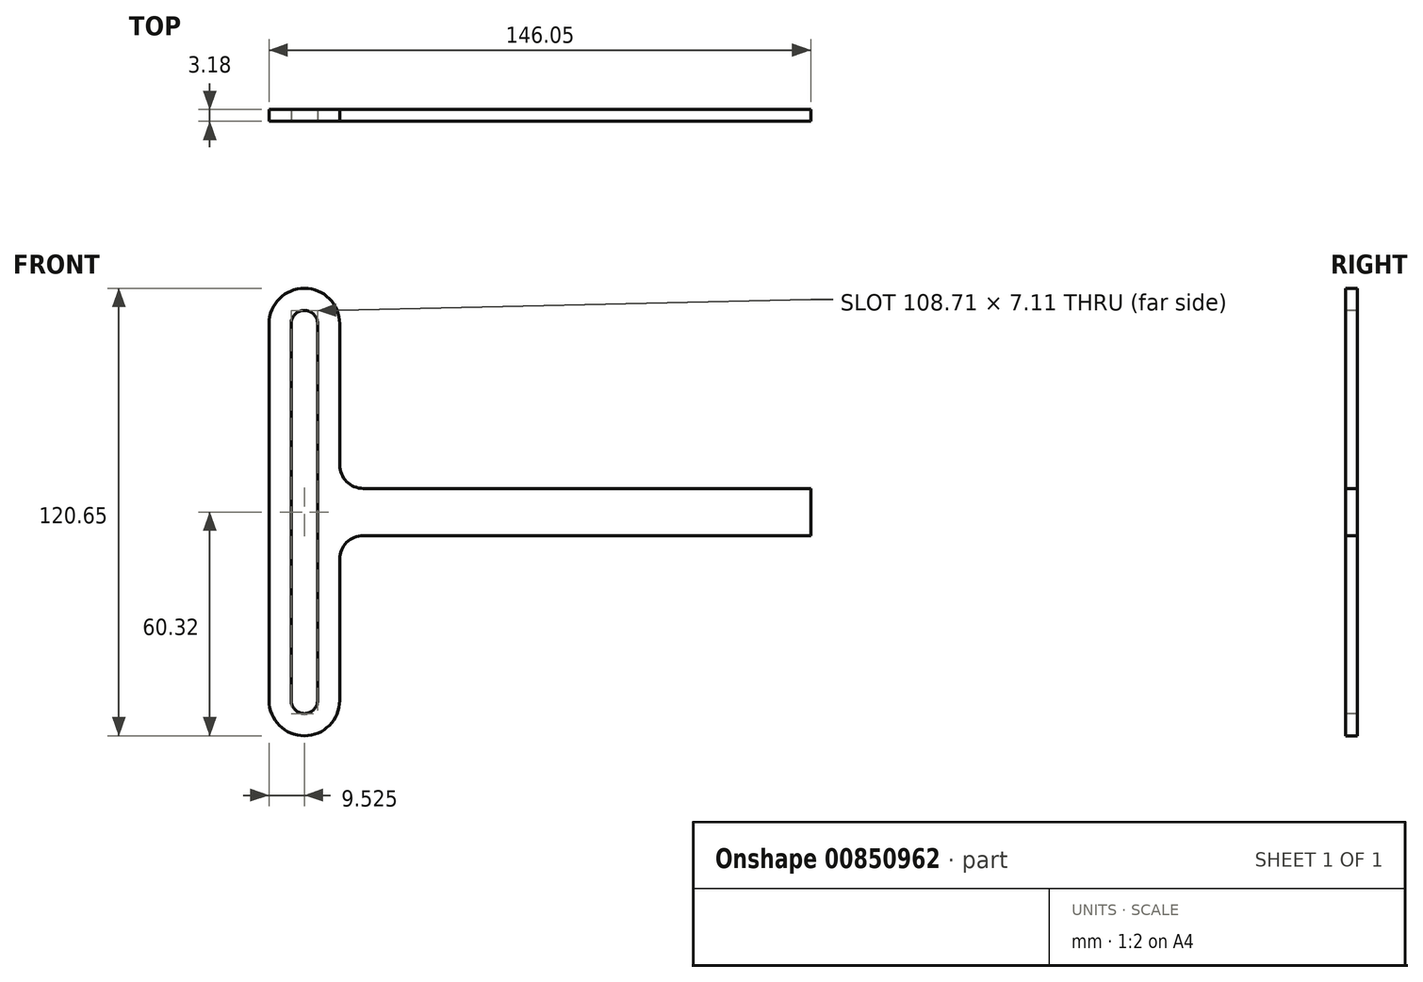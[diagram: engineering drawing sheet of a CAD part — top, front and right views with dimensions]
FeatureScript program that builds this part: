
annotation { "Feature Type Name" : "Feature", "Feature Type Description" : "" }
export const myFeature = defineFeature(function(context is Context, id is Id, definition is map)
    precondition{}
    {
        {
            var Q0;
            Q0=qCreatedBy(makeId("Front.planeOp"),FACE);
            var sketch = newSketch(context, id + "F0", { "sketchPlane" : qUnion([Q0])});
            skLineSegment(sketch, "E0.bottom", {"start": v(6.35, 0) * mm, "end": v(127, 0) * mm});
            skLineSegment(sketch, "E0.top", {"start": v(6.35, -12.7) * mm, "end": v(127, -12.7) * mm});
            skLineSegment(sketch, "E0.right", {"start": v(127, 0) * mm, "end": v(127, -12.7) * mm});
            skLineSegment(sketch, "E1", {"start": v(0, 6.35) * mm, "end": v(0, 44.45) * mm});
            skLineSegment(sketch, "E2", {"start": v(-19.05, 44.45) * mm, "end": v(-19.05, -57.15) * mm});
            skLineSegment(sketch, "E3", {"start": v(0, -57.15) * mm, "end": v(0, -19.05) * mm});
            skArc(sketch, "E4", {"start": v(0, 44.45) * mm, "mid": v(-9.52, 53.98) * mm, "end": v(-19.05, 44.45) * mm});
            skArc(sketch, "E5", {"start": v(-19.05, -57.15) * mm, "mid": v(-9.52, -66.68) * mm, "end": v(0, -57.15) * mm});
            skPoint(sketch, "E6.visualSharp", {"position": v(0, 0) * mm});
            skArc(sketch, "E6.filletArc", {"start": v(0, 6.35) * mm, "mid": v(1.86, 1.86) * mm, "end": v(6.35, 0) * mm});
            skPoint(sketch, "E7.visualSharp", {"position": v(0, -12.7) * mm});
            skArc(sketch, "E7.filletArc", {"start": v(6.35, -12.7) * mm, "mid": v(1.86, -14.56) * mm, "end": v(0, -19.05) * mm});
            skSolve(sketch);
        }
        {
            var Q0;
            Q0 = qSketchRegion(id + "F0", true);
            extrude(context, id + "F1", {"entities" : qUnion([Q0]), "depth" : 3.17 * mm, "offsetDistance" : 25.4 * mm});
        }
        {
            var Q0;
            Q0=makeQuery(id+"F1.opExtrude","CAP_FACE",FACE,{"disambiguationData":[OSD([sQuery(id+"F0.wireOp",EDGE,"E0.bottom"),sQuery(id+"F0.wireOp",EDGE,"E0.top"),sQuery(id+"F0.wireOp",EDGE,"E0.right"),sQuery(id+"F0.wireOp",EDGE,"E1"),sQuery(id+"F0.wireOp",EDGE,"E2"),sQuery(id+"F0.wireOp",EDGE,"E3"),sQuery(id+"F0.wireOp",EDGE,"E4"),sQuery(id+"F0.wireOp",EDGE,"E5"),sQuery(id+"F0.wireOp",EDGE,"E6.filletArc"),sQuery(id+"F0.wireOp",EDGE,"E7.filletArc")])],"isStart":false});
            var sketch = newSketch(context, id + "F2", { "sketchPlane" : qUnion([Q0])});
            skArc(sketch, "E8.0", {"start": v(-5.97, 44.45) * mm, "mid": v(-9.52, 48) * mm, "end": v(-13.08, 44.45) * mm});
            skLineSegment(sketch, "E8.1", {"start": v(-5.97, 6.35) * mm, "end": v(-5.97, 44.45) * mm});
            skLineSegment(sketch, "E8.2", {"start": v(-13.08, 44.45) * mm, "end": v(-13.08, -57.15) * mm});
            skArc(sketch, "E8.6", {"start": v(-13.08, -57.15) * mm, "mid": v(-9.52, -60.7) * mm, "end": v(-5.97, -57.15) * mm});
            skLineSegment(sketch, "E8.7", {"start": v(-5.97, -57.15) * mm, "end": v(-5.97, -19.05) * mm});
            skLineSegment(sketch, "E9", {"start": v(-5.97, 6.35) * mm, "end": v(-5.97, -19.05) * mm});
            skSolve(sketch);
        }
        {
            var Q0;
            Q0 = qSketchRegion(id + "F2", true);
            extrude(context, id + "F3", {"entities" : qUnion([Q0]), "operationType" : NewBodyOperationType.REMOVE, "oppositeDirection" : true, "depth" : 25.4 * mm, "offsetDistance" : 25.4 * mm});
        }
    });
